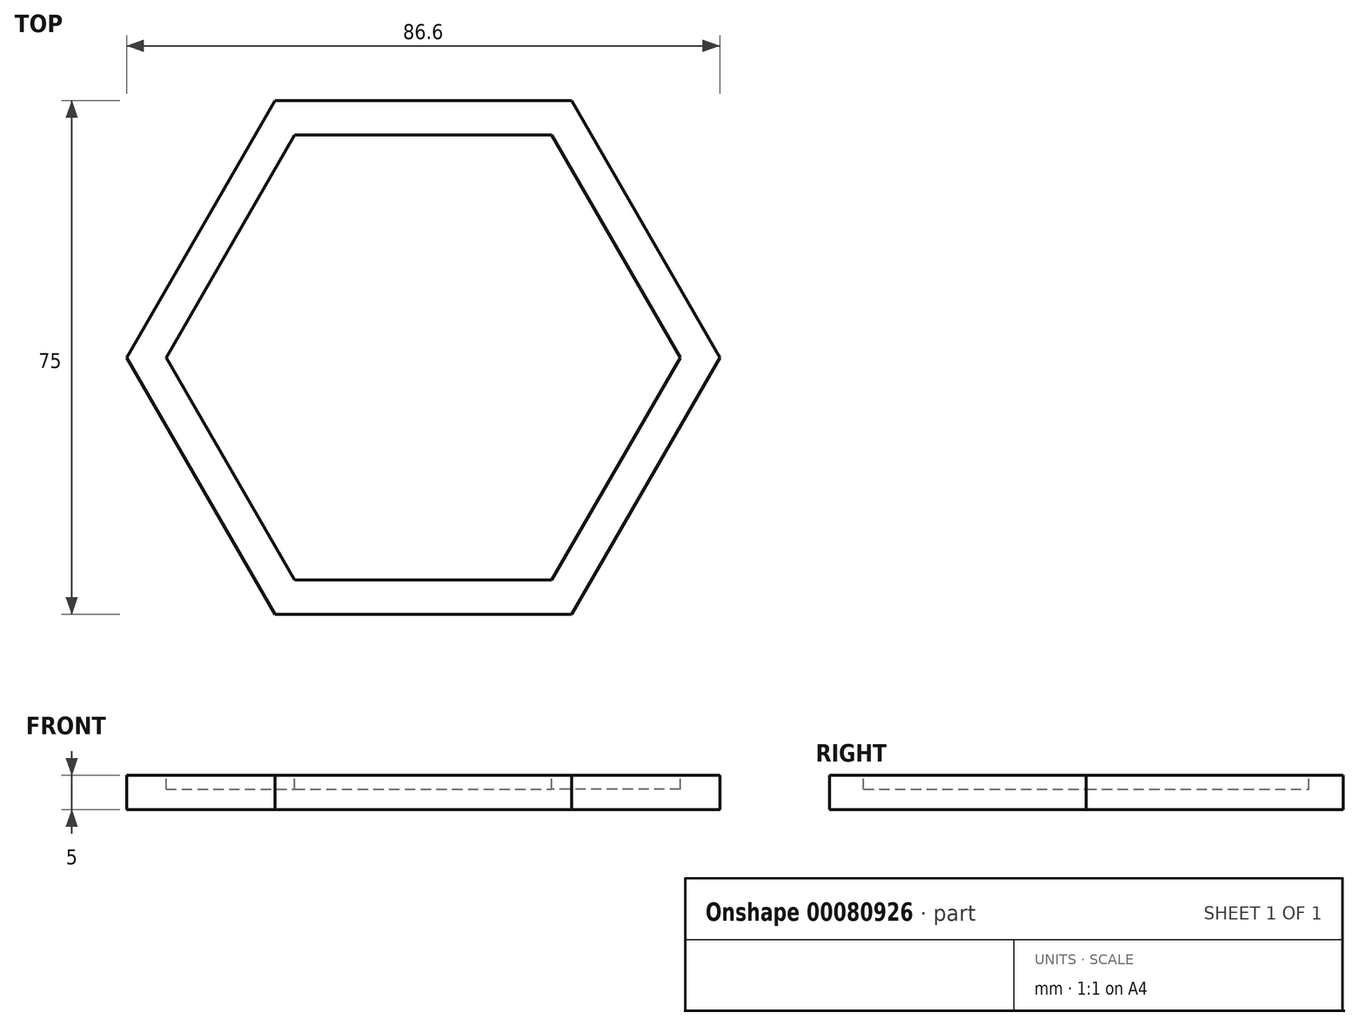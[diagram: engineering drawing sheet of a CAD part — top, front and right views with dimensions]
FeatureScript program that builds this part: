
annotation { "Feature Type Name" : "Feature", "Feature Type Description" : "" }
export const myFeature = defineFeature(function(context is Context, id is Id, definition is map)
    precondition{}
    {
        {
            var Q0;
            Q0=qCreatedBy(makeId("Top.planeOp"),FACE);
            var sketch = newSketch(context, id + "F0", { "sketchPlane" : qUnion([Q0])});
            skCircle(sketch, "E0.cCircle", {"center": v(0, 0) * mm, "radius": 37.5 * mm, "construction": true});
            skLineSegment(sketch, "E0.0", {"start": v(-21.65, 37.5) * mm, "end": v(21.65, 37.5) * mm});
            skLineSegment(sketch, "E0.1", {"start": v(21.65, 37.5) * mm, "end": v(43.3, 0) * mm});
            skLineSegment(sketch, "E0.2", {"start": v(43.3, 0) * mm, "end": v(21.65, -37.5) * mm});
            skLineSegment(sketch, "E0.3", {"start": v(21.65, -37.5) * mm, "end": v(-21.65, -37.5) * mm});
            skLineSegment(sketch, "E0.4", {"start": v(-21.65, -37.5) * mm, "end": v(-43.3, 0) * mm});
            skLineSegment(sketch, "E0.5", {"start": v(-43.3, 0) * mm, "end": v(-21.65, 37.5) * mm});
            skPoint(sketch, "E0.0.midPoint", {"position": v(0, 37.5) * mm});
            skSolve(sketch);
        }
        {
            var Q0;
            Q0 = qSketchRegion(id + "F0", true);
            extrude(context, id + "F1", {"entities" : qUnion([Q0]), "depth" : 5 * mm});
        }
        {
            var Q0;
            Q0=makeQuery(id+"F1.opExtrude","CAP_FACE",FACE,{"disambiguationData":[OSD([sQuery(id+"F0.wireOp",EDGE,"E0.0"),sQuery(id+"F0.wireOp",EDGE,"E0.1"),sQuery(id+"F0.wireOp",EDGE,"E0.2"),sQuery(id+"F0.wireOp",EDGE,"E0.3"),sQuery(id+"F0.wireOp",EDGE,"E0.4"),sQuery(id+"F0.wireOp",EDGE,"E0.5")])],"isStart":false});
            var sketch = newSketch(context, id + "F2", { "sketchPlane" : qUnion([Q0])});
            skCircle(sketch, "E1.cCircle", {"center": v(0, 0) * mm, "radius": 32.5 * mm, "construction": true});
            skLineSegment(sketch, "E1.0", {"start": v(-18.76, 32.5) * mm, "end": v(18.76, 32.5) * mm});
            skLineSegment(sketch, "E1.1", {"start": v(18.76, 32.5) * mm, "end": v(37.53, 0) * mm});
            skLineSegment(sketch, "E1.2", {"start": v(37.53, 0) * mm, "end": v(18.76, -32.5) * mm});
            skLineSegment(sketch, "E1.3", {"start": v(18.76, -32.5) * mm, "end": v(-18.76, -32.5) * mm});
            skLineSegment(sketch, "E1.4", {"start": v(-18.76, -32.5) * mm, "end": v(-37.53, 0) * mm});
            skLineSegment(sketch, "E1.5", {"start": v(-37.53, 0) * mm, "end": v(-18.76, 32.5) * mm});
            skPoint(sketch, "E1.0.midPoint", {"position": v(0, 32.5) * mm});
            skSolve(sketch);
        }
        {
            var Q0;
            Q0 = qSketchRegion(id + "F2", true);
            extrude(context, id + "F3", {"entities" : qUnion([Q0]), "operationType" : NewBodyOperationType.REMOVE, "oppositeDirection" : true, "depth" : 2 * mm});
        }
    });
